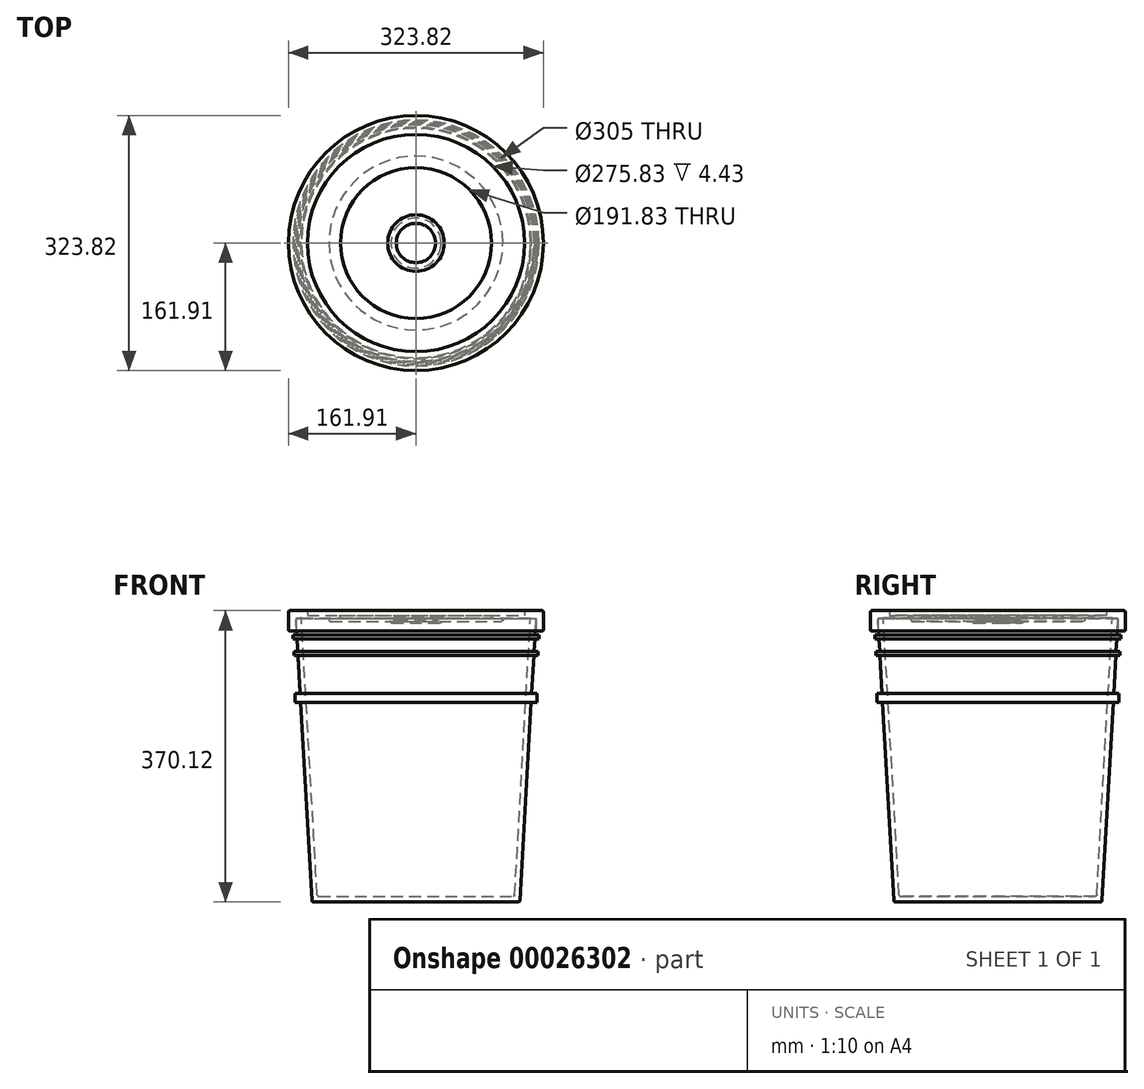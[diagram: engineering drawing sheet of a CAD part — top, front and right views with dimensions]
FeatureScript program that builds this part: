
annotation { "Feature Type Name" : "Feature", "Feature Type Description" : "" }
export const myFeature = defineFeature(function(context is Context, id is Id, definition is map)
    precondition{}
    {
        {
            var Q0;
            Q0=qCreatedBy(makeId("Front.planeOp"),FACE);
            var sketch = newSketch(context, id + "F0", { "sketchPlane" : qUnion([Q0])});
            skLineSegment(sketch, "E0", {"start": v(0, 0) * mm, "end": v(130.11, 0) * mm});
            skLineSegment(sketch, "E1", {"start": v(132.1, 1.89) * mm, "end": v(152.5, 360) * mm});
            skLineSegment(sketch, "E2", {"start": v(0, 0) * mm, "end": v(0, 360) * mm, "construction": true});
            skLineSegment(sketch, "E3", {"start": v(-148.45, 360) * mm, "end": v(239.8, 360) * mm, "construction": true});
            skLineSegment(sketch, "E4", {"start": v(151.32, 339.27) * mm, "end": v(156.32, 339.27) * mm});
            skLineSegment(sketch, "E5", {"start": v(156.32, 339.27) * mm, "end": v(156.32, 334.27) * mm});
            skLineSegment(sketch, "E6", {"start": v(156.32, 334.27) * mm, "end": v(151.03, 334.27) * mm});
            skLineSegment(sketch, "E7", {"start": v(150.12, 318.2) * mm, "end": v(155.12, 318.2) * mm});
            skLineSegment(sketch, "E8", {"start": v(155.12, 318.2) * mm, "end": v(155.12, 313.2) * mm});
            skLineSegment(sketch, "E9", {"start": v(155.12, 313.2) * mm, "end": v(149.84, 313.2) * mm});
            skLineSegment(sketch, "E10.0", {"start": v(125.5, 8.89) * mm, "end": v(145.52, 360.6) * mm});
            skLineSegment(sketch, "E10.1", {"start": v(0, 7) * mm, "end": v(123.5, 7) * mm});
            skLineSegment(sketch, "E11", {"start": v(145.52, 360.6) * mm, "end": v(152.5, 360) * mm});
            skLineSegment(sketch, "E12", {"start": v(0, 7) * mm, "end": v(0, 0) * mm});
            skLineSegment(sketch, "E13", {"start": v(147.08, 264.84) * mm, "end": v(153.8, 264.84) * mm});
            skLineSegment(sketch, "E14", {"start": v(153.8, 264.84) * mm, "end": v(153.8, 253.45) * mm});
            skLineSegment(sketch, "E15", {"start": v(153.8, 253.45) * mm, "end": v(146.43, 253.45) * mm});
            skLineSegment(sketch, "E16", {"start": v(152.5, 360) * mm, "end": v(152.5, 346.1) * mm});
            skLineSegment(sketch, "E17", {"start": v(154.5, 344.1) * mm, "end": v(159.91, 344.1) * mm});
            skLineSegment(sketch, "E18", {"start": v(161.91, 346.1) * mm, "end": v(161.91, 368.12) * mm});
            skLineSegment(sketch, "E19", {"start": v(159.91, 370.12) * mm, "end": v(139.91, 370.12) * mm});
            skLineSegment(sketch, "E20", {"start": v(137.91, 368.12) * mm, "end": v(137.91, 363.7) * mm});
            skLineSegment(sketch, "E21", {"start": v(137.91, 363.7) * mm, "end": v(97.91, 363.7) * mm});
            skLineSegment(sketch, "E22", {"start": v(95.91, 361.7) * mm, "end": v(95.91, 361.66) * mm});
            skLineSegment(sketch, "E23", {"start": v(94.91, 360.66) * mm, "end": v(35.91, 360.66) * mm});
            skLineSegment(sketch, "E24", {"start": v(25, 357.8) * mm, "end": v(0, 357.8) * mm});
            skLineSegment(sketch, "E25", {"start": v(0, 357.8) * mm, "end": v(0, 354.29) * mm});
            skLineSegment(sketch, "E26", {"start": v(0, 354.29) * mm, "end": v(30.8, 354.29) * mm});
            skLineSegment(sketch, "E27", {"start": v(31.8, 355.29) * mm, "end": v(31.8, 355.56) * mm});
            skLineSegment(sketch, "E28", {"start": v(32.8, 356.56) * mm, "end": v(108.5, 356.56) * mm});
            skLineSegment(sketch, "E29", {"start": v(110.5, 358.56) * mm, "end": v(110.5, 359) * mm});
            skLineSegment(sketch, "E30", {"start": v(111.5, 360) * mm, "end": v(145.49, 360) * mm});
            skLineSegment(sketch, "E31", {"start": v(145.49, 360) * mm, "end": v(145.52, 361.82) * mm});
            skLineSegment(sketch, "E32", {"start": v(145.52, 361.82) * mm, "end": v(152.62, 361.69) * mm});
            skLineSegment(sketch, "E33", {"start": v(152.62, 361.69) * mm, "end": v(152.51, 360) * mm});
            skPoint(sketch, "E34.visualSharp", {"position": v(137.91, 370.12) * mm});
            skArc(sketch, "E34.filletArc", {"start": v(139.91, 370.12) * mm, "mid": v(138.5, 369.54) * mm, "end": v(137.91, 368.12) * mm});
            skPoint(sketch, "E35.visualSharp", {"position": v(161.91, 370.12) * mm});
            skArc(sketch, "E35.filletArc", {"start": v(161.91, 368.12) * mm, "mid": v(161.33, 369.54) * mm, "end": v(159.91, 370.12) * mm});
            skPoint(sketch, "E36.visualSharp", {"position": v(95.91, 363.7) * mm});
            skArc(sketch, "E36.filletArc", {"start": v(97.91, 363.7) * mm, "mid": v(96.5, 363.1) * mm, "end": v(95.91, 361.7) * mm});
            skPoint(sketch, "E37.visualSharp", {"position": v(110.5, 356.56) * mm});
            skArc(sketch, "E37.filletArc", {"start": v(108.5, 356.56) * mm, "mid": v(109.9, 357.14) * mm, "end": v(110.5, 358.56) * mm});
            skPoint(sketch, "E38.visualSharp", {"position": v(152.5, 344.1) * mm});
            skArc(sketch, "E38.filletArc", {"start": v(152.5, 346.1) * mm, "mid": v(153.09, 344.69) * mm, "end": v(154.5, 344.1) * mm});
            skPoint(sketch, "E39.visualSharp", {"position": v(161.91, 344.1) * mm});
            skArc(sketch, "E39.filletArc", {"start": v(159.91, 344.1) * mm, "mid": v(161.33, 344.69) * mm, "end": v(161.91, 346.1) * mm});
            skPoint(sketch, "E40.visualSharp", {"position": v(132, 0) * mm});
            skArc(sketch, "E40.filletArc", {"start": v(130.11, 0) * mm, "mid": v(131.48, 0.55) * mm, "end": v(132.1, 1.89) * mm});
            skPoint(sketch, "E41.visualSharp", {"position": v(125.39, 7) * mm});
            skArc(sketch, "E41.filletArc", {"start": v(123.5, 7) * mm, "mid": v(124.87, 7.55) * mm, "end": v(125.5, 8.89) * mm});
            skFitSpline(sketch, "E42", {"points": [v(35.91, 360.66) * mm, v(30.57, 360.66) * mm, v(29.46, 360) * mm, v(28.34, 358.54) * mm, v(25, 357.8) * mm], "startDerivative": vector(-9.5, 1.35) * mm, "endDerivative": vector(-13.2, -1.22) * mm});
            skPoint(sketch, "E43.visualSharp", {"position": v(95.91, 360.66) * mm});
            skArc(sketch, "E43.filletArc", {"start": v(94.91, 360.66) * mm, "mid": v(95.62, 360.96) * mm, "end": v(95.91, 361.66) * mm});
            skPoint(sketch, "E44.visualSharp", {"position": v(31.8, 354.29) * mm});
            skArc(sketch, "E44.filletArc", {"start": v(30.8, 354.29) * mm, "mid": v(31.5, 354.58) * mm, "end": v(31.8, 355.29) * mm});
            skPoint(sketch, "E45.visualSharp", {"position": v(31.8, 356.56) * mm});
            skArc(sketch, "E45.filletArc", {"start": v(32.8, 356.56) * mm, "mid": v(32.1, 356.27) * mm, "end": v(31.8, 355.56) * mm});
            skPoint(sketch, "E46.visualSharp", {"position": v(110.5, 360) * mm});
            skArc(sketch, "E46.filletArc", {"start": v(111.5, 360) * mm, "mid": v(110.78, 359.7) * mm, "end": v(110.5, 359) * mm});
            skSolve(sketch);
        }
        {
            var Q0;
            {var subQ8=sQuery(id+"F0.wireOp",EDGE,"E0");Q0=makeQuery(id+"F0.imprint","IMPRINT",FACE,{"disambiguationData":[TD([[makeQuery(id+"F0.imprint","IMPRINT",EDGE,{"derivedFrom":subQ8}),1.0]])]});}
            var Q1;
            {var subQ1=sQuery(id+"F0.wireOp",EDGE,"E13");Q1=makeQuery(id+"F0.imprint","IMPRINT",FACE,{"disambiguationData":[TD([[makeQuery(id+"F0.imprint","IMPRINT",EDGE,{"derivedFrom":subQ1}),-1.0]])]});}
            var Q2;
            {var subQ1=sQuery(id+"F0.wireOp",EDGE,"E7");Q2=makeQuery(id+"F0.imprint","IMPRINT",FACE,{"disambiguationData":[TD([[makeQuery(id+"F0.imprint","IMPRINT",EDGE,{"derivedFrom":subQ1}),-1.0]])]});}
            var Q3;
            {var subQ1=sQuery(id+"F0.wireOp",EDGE,"E4");Q3=makeQuery(id+"F0.imprint","IMPRINT",FACE,{"disambiguationData":[TD([[makeQuery(id+"F0.imprint","IMPRINT",EDGE,{"derivedFrom":subQ1}),-1.0]])]});}
            var Q4;
            Q4=sQuery(id+"F0.wireOp",EDGE,"E2");
            revolve(context, id + "F1", {"entities" : qUnion([Q0, Q1, Q2, Q3]), "axis" : qUnion([Q4]), "revolveType" : RevolveType.FULL});
        }
        {
            var Q0;
            {var subQ2=sQuery(id+"F0.wireOp",EDGE,"E11");Q0=makeQuery(id+"F0.imprint","IMPRINT",FACE,{"disambiguationData":[TD([[makeQuery(id+"F0.imprint","IMPRINT",EDGE,{"derivedFrom":subQ2}),1.0]])]});}
            var Q1;
            Q1=sQuery(id+"F0.wireOp",EDGE,"E2");
            revolve(context, id + "F2", {"entities" : qUnion([Q0]), "axis" : qUnion([Q1]), "revolveType" : RevolveType.FULL});
        }
    });
